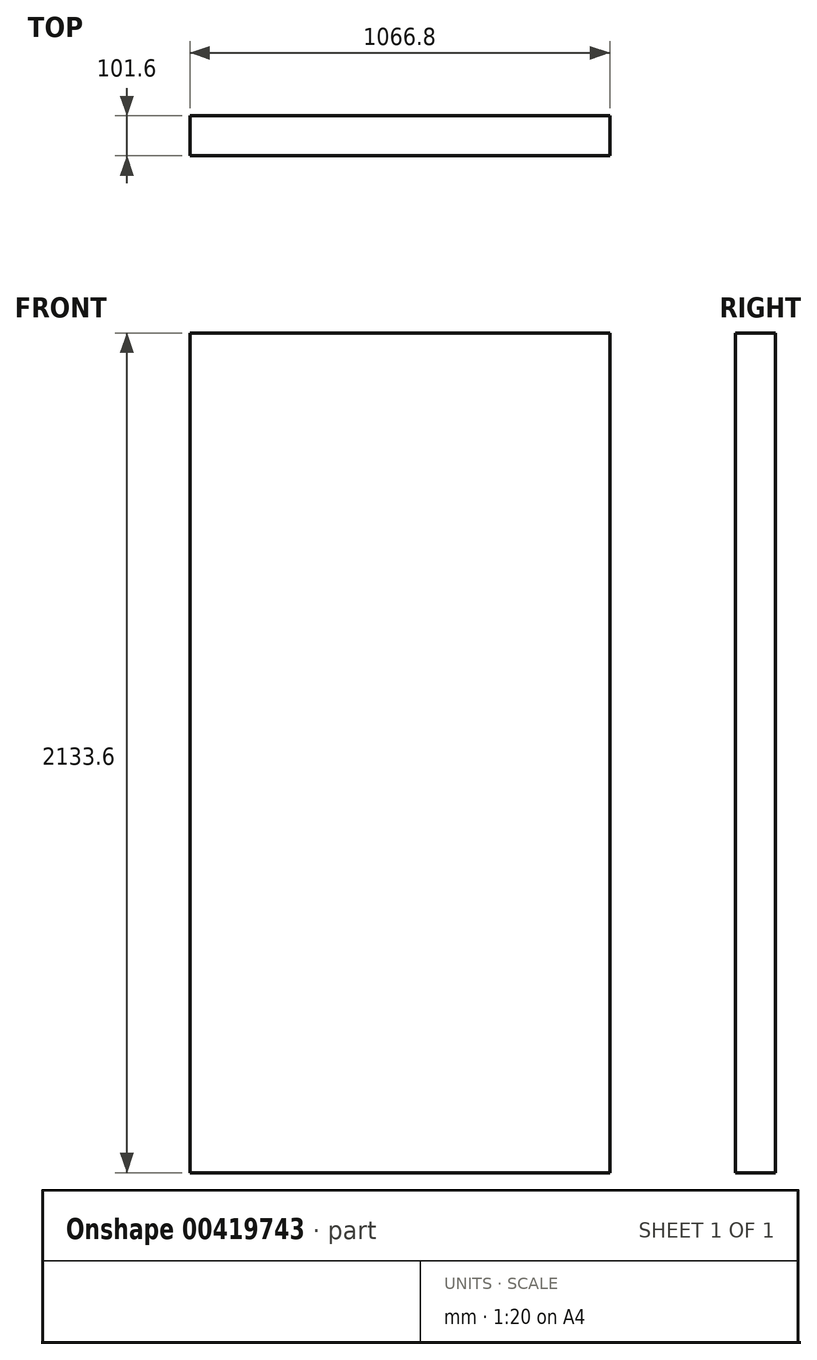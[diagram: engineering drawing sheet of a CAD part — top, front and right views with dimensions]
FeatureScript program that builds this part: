
annotation { "Feature Type Name" : "Feature", "Feature Type Description" : "" }
export const myFeature = defineFeature(function(context is Context, id is Id, definition is map)
    precondition{}
    {
        {
            var Q0;
            Q0=qCreatedBy(makeId("Front.planeOp"),FACE);
            var sketch = newSketch(context, id + "F0", { "sketchPlane" : qUnion([Q0])});
            skLineSegment(sketch, "E0", {"start": v(-490.93, 1067.56) * mm, "end": v(-490.93, -1066.04) * mm});
            skLineSegment(sketch, "E1", {"start": v(-490.93, -1066.04) * mm, "end": v(575.87, -1066.04) * mm});
            skLineSegment(sketch, "E2", {"start": v(575.87, -1066.04) * mm, "end": v(575.87, 1067.56) * mm});
            skLineSegment(sketch, "E3", {"start": v(575.87, 1067.56) * mm, "end": v(-490.93, 1067.56) * mm});
            skSolve(sketch);
        }
        {
            var Q0;
            Q0=makeQuery(id+"F0.imprint","IMPRINT",FACE,{"disambiguationData":[TD([[makeQuery(id+"F0.imprint","IMPRINT",EDGE,{"derivedFrom":sQuery(id+"F0.wireOp",EDGE,"E0")}),1.0]])]});
            extrude(context, id + "F1", {"entities" : qUnion([Q0]), "depth" : 101.6 * mm});
        }
    });
